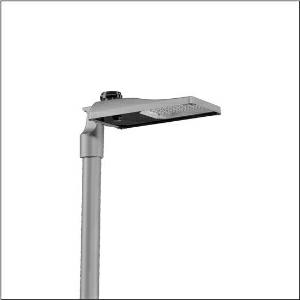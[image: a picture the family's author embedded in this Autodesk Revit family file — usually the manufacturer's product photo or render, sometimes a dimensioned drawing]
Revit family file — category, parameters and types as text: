
# Revit family: streetlight_sl_31_mini___st1_0a_5xh2d35m08ha_81d0
name_source: partatom
category: Lighting Fixtures
units: mm (PartAtom-declared; Revit-internal decimal feet)

## family parameters
Cut with Voids When Loaded = No
Host = Face
Light Source = No
Part Type = Normal
Room Calculation Point = No
Round Connector Dimension = Use Diameter
Shared = No

## types (1)
- --- (1 x LED, 9230 lm, 68.3 W, 3000K)
    Apparent Load = 68 VA
    CIE Flux Codes = 37 72 97 100 100
    Color Rendering = 70
    Color Temperature = 3000K
    Default Elevation = 1800 mm
    Description = Streetlight SL 31 mini NEMA (7pin), Desk-Remote mast luminaire for post-top, side-entry; light control with lens of PMMA; light distribution: ST1.0a, direct asymmetric distribution, for standard-compliant lighting for roads and squares; LED: luminous flux: 9.230lm, light colour: 730, colour temperature: 3000K; luminous efficacy: 135,3lm/W; control: pre-setting: linear dimming characteristic, flexible luminous flux parameterisation, time-dependent luminous flux control, constant luminous flux control, intelligent temperature release in ECG and LED module, overheat protection; luminaire housing, of diecast aluminium, Siteco® metallic grey (DB 702S), corrosivity category C5 high according to DIN EN ISO 12944; cover of toughened safety glass, transparent, mast flange of diecast aluminium, Siteco® metallic grey (DB 702S), spigot size: 76/60mm, mast flange included unmounted; with cable H07RN-F 3x 1.5mm², cable length: 8,5m, connection cable pre-assembled; mains connection: 220..240V, AC, 50/60Hz; power consumption (at start of service life): 68,2W / (at end of service life): 74,4W / (with reduced operation 50%): 29,7W; protection rating (complete): IP66; insulation class (complete): insulation class I (protective earthing); impact resistance: IK09; certification: CE, ENEC, ENEC+, VDE, UKCA; permissible operating ambient temperature for outdoor applications: -40..+50°C; packaging unit: 1 piece

Light Distribution: ST1.0a
    Height = 76 mm
    Lamp = 1 x LED
    Lamp Light Flux = 9230 lm
    Lamp Power = 68.3 W
    Lamp count = 1
    Length = 547 mm
    Luminous efficacy = 135 lm/W
    Manufacturer = Siteco
    ModVariant = No
    Model = 5XH2D35M08HA
    Number of Poles = 1
    OnlyDefault = Yes
    Power Factor = 1
    Product Name = Streetlight SL 31 mini | ST1.0a
    Product group = mast luminaire | pylon top
    ProductGroupID = 6100
    Protection Class = Protection class I
    Protection Degree = IP 66
    RLX_Detail_Level = 1
    RLX_Emergency_Light_Flux = 0 lm
    RLX_Emergency_Type = 0
    RLX_Emergency_Type_DB = No
    RlxData = <blob elided: 24829 chars, md5=59f1533f>
    Socket = socket
    Standby Power = 0 W
    System Light Flux = 9230 lm
    System Power = 68 W
    Type Comments = factory setting: luminous flux: 100 % | dim-lin: 254 | 692 mA
    Type Image = l_1300324.jpg
    URL = http://relux.com
    VarID = @adj_002691
    Voltage = 0 V
    Weight = 0.00 kg
    Width = 265 mm

## geometry (parser evidence)
native form markers: Blend x4, Sweep x11
no freeform markers — native parametric forms only
